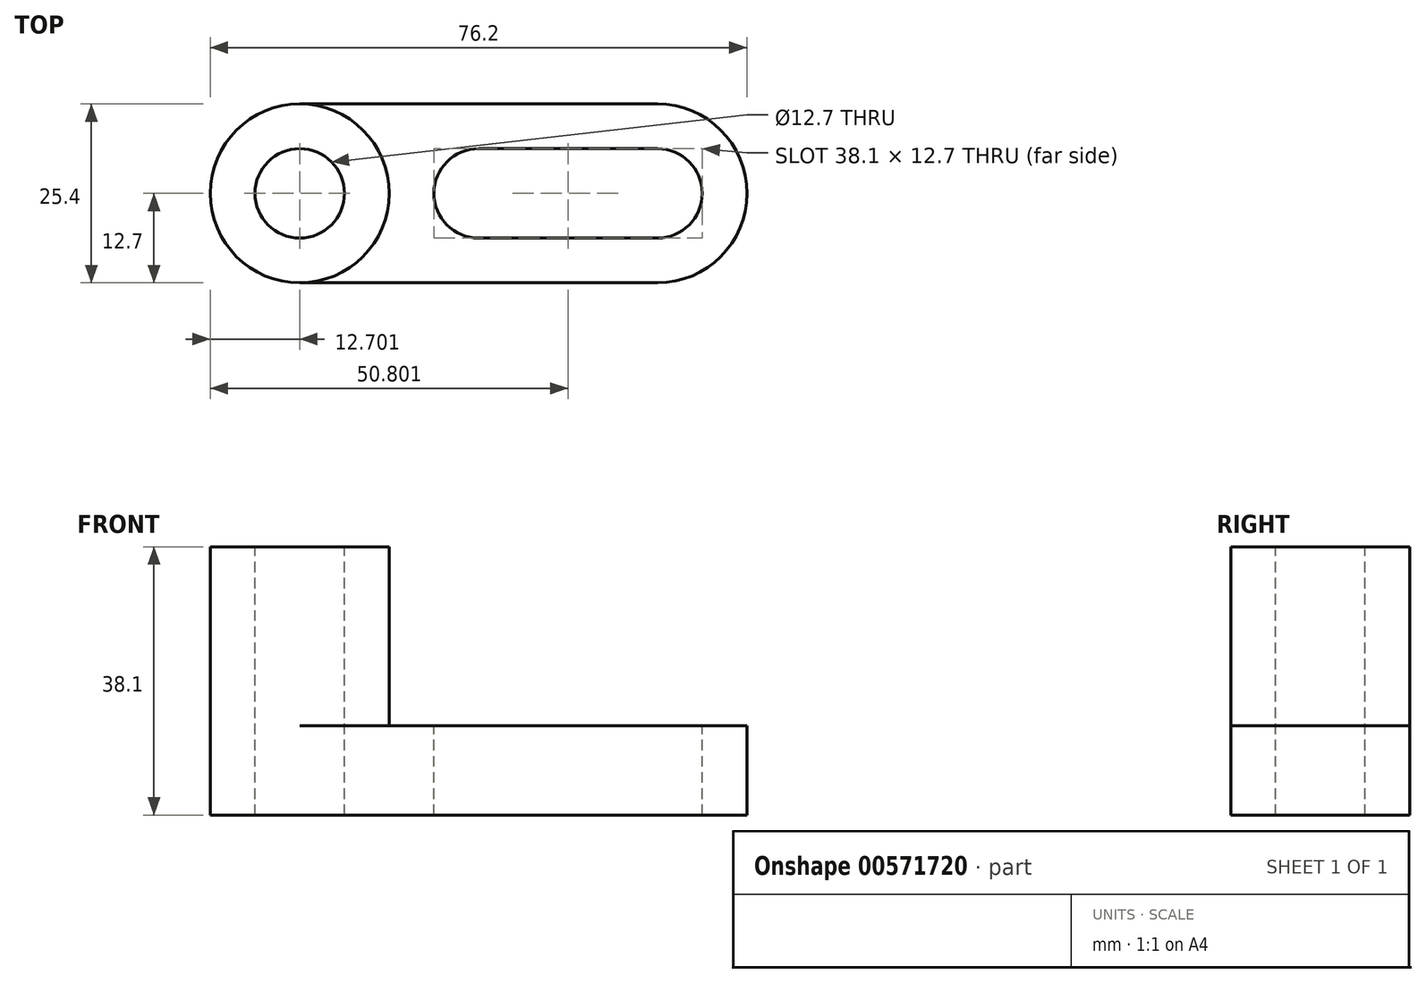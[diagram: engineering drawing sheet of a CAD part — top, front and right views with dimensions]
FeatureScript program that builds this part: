
annotation { "Feature Type Name" : "Feature", "Feature Type Description" : "" }
export const myFeature = defineFeature(function(context is Context, id is Id, definition is map)
    precondition{}
    {
        {
            var Q0;
            Q0=qCreatedBy(makeId("Front.planeOp"),FACE);
            var sketch = newSketch(context, id + "F0", { "sketchPlane" : qUnion([Q0])});
            skLineSegment(sketch, "E0", {"start": v(-41.4, 37.42) * mm, "end": v(9.4, 37.42) * mm});
            skLineSegment(sketch, "E1", {"start": v(9.4, 37.42) * mm, "end": v(9.4, 24.72) * mm});
            skLineSegment(sketch, "E2", {"start": v(9.4, 24.72) * mm, "end": v(-41.4, 24.72) * mm});
            skLineSegment(sketch, "E3", {"start": v(-41.4, 24.72) * mm, "end": v(-41.4, 37.42) * mm});
            skSolve(sketch);
        }
        {
            var Q0;
            Q0=makeQuery(id+"F0.imprint","IMPRINT",FACE,{"disambiguationData":[TD([[makeQuery(id+"F0.imprint","IMPRINT",EDGE,{"derivedFrom":sQuery(id+"F0.wireOp",EDGE,"E0")}),-1.0]])]});
            extrude(context, id + "F1", {"entities" : qUnion([Q0]), "depth" : 25.4 * mm, "offsetDistance" : 25.4 * mm});
        }
        {
            var Q0;
            Q0=makeQuery(id+"F1.opExtrude","SWEPT_FACE",FACE,{"disambiguationData":[OSD([sQuery(id+"F0.wireOp",EDGE,"E0")])]});
            var sketch = newSketch(context, id + "F2", { "sketchPlane" : qUnion([Q0])});
            skArc(sketch, "E4", {"start": v(9.4, -25.4) * mm, "mid": v(22.1, -12.7) * mm, "end": v(9.4, 0) * mm});
            skArc(sketch, "E5", {"start": v(-41.4, 0) * mm, "mid": v(-54.1, -12.7) * mm, "end": v(-41.4, -25.4) * mm});
            skCircle(sketch, "E6", {"center": v(-41.4, -12.7) * mm, "radius": 12.7 * mm});
            skSolve(sketch);
        }
        {
            var Q0;
            Q0=makeQuery(id+"F2.imprint","IMPRINT",FACE,{"disambiguationData":[TD([[makeQuery(id+"F2.imprint","IMPRINT",EDGE,{"derivedFrom":sQuery(id+"F2.wireOp",EDGE,"E4")}),1.0]])]});
            var Q1;
            {var subQ1=sQuery(id+"F0.wireOp",EDGE,"E0");var subQ2=makeQuery(id+"F1.opExtrude","SWEPT_EDGE",EDGE,{"disambiguationData":[OSD([subQ1,sQuery(id+"F0.wireOp",EDGE,"E3")])]});Q1=makeQuery(id+"F2.imprint","IMPRINT",FACE,{"disambiguationData":[TD([[makeQuery(id+"F2.imprint","IMPRINT",EDGE,{"derivedFrom":subQ2}),1.0]])]});}
            extrude(context, id + "F3", {"entities" : qUnion([Q0, Q1]), "operationType" : NewBodyOperationType.ADD, "oppositeDirection" : true, "depth" : 12.7 * mm, "offsetDistance" : 25.4 * mm});
        }
        {
            var Q0;
            Q0 = qSketchRegion(id + "F2", true);
            extrude(context, id + "F4", {"entities" : qUnion([Q0]), "operationType" : NewBodyOperationType.ADD, "depth" : 25.4 * mm, "offsetDistance" : 25.4 * mm});
        }
        {
            var Q0;
            Q0=makeQuery(id+"F4.opExtrude","CAP_FACE",FACE,{"disambiguationData":[OSD([sQuery(id+"F2.wireOp",EDGE,"E6")])],"isStart":false});
            var sketch = newSketch(context, id + "F5", { "sketchPlane" : qUnion([Q0])});
            skCircle(sketch, "E7", {"center": v(-41.4, -12.7) * mm, "radius": 6.35 * mm});
            skSolve(sketch);
        }
        {
            var Q0;
            Q0 = qSketchRegion(id + "F5", true);
            extrude(context, id + "F6", {"entities" : qUnion([Q0]), "operationType" : NewBodyOperationType.REMOVE, "oppositeDirection" : true, "depth" : 2514.6 * mm, "offsetDistance" : 25.4 * mm});
        }
        {
            var Q0;
            {var subQ0=sQuery(id+"F0.wireOp",EDGE,"E0");Q0=makeQuery(id+"F3.boolean.opBoolean","MERGE",FACE,{"derivedFrom":[makeQuery(id+"F1.opExtrude","SWEPT_FACE",FACE,{"disambiguationData":[OSD([subQ0])]}),makeQuery(id+"F3.opExtrude","CAP_FACE",FACE,{"disambiguationData":[OSD([subQ0,sQuery(id+"F0.wireOp",EDGE,"E1"),sQuery(id+"F2.wireOp",EDGE,"E4")])],"isStart":true}),makeQuery(id+"F3.opExtrude","CAP_FACE",FACE,{"disambiguationData":[OSD([subQ0,sQuery(id+"F0.wireOp",EDGE,"E3"),sQuery(id+"F2.wireOp",EDGE,"E6")])],"isStart":true})]});}
            var sketch = newSketch(context, id + "F7", { "sketchPlane" : qUnion([Q0])});
            skLineSegment(sketch, "E8", {"start": v(-16, -19.05) * mm, "end": v(9.4, -19.05) * mm});
            skLineSegment(sketch, "E9", {"start": v(-16, -19.05) * mm, "end": v(-16, -6.35) * mm});
            skLineSegment(sketch, "E10", {"start": v(-16, -6.35) * mm, "end": v(9.4, -6.35) * mm});
            skLineSegment(sketch, "E11", {"start": v(9.4, -6.35) * mm, "end": v(9.4, -19.05) * mm});
            skArc(sketch, "E12", {"start": v(-16, -6.35) * mm, "mid": v(-22.35, -12.7) * mm, "end": v(-16, -19.05) * mm});
            skArc(sketch, "E13", {"start": v(9.4, -19.05) * mm, "mid": v(15.75, -12.7) * mm, "end": v(9.4, -6.35) * mm});
            skSolve(sketch);
        }
        {
            var Q0;
            Q0=makeQuery(id+"F7.imprint","IMPRINT",FACE,{"disambiguationData":[TD([[makeQuery(id+"F7.imprint","IMPRINT",EDGE,{"derivedFrom":sQuery(id+"F7.wireOp",EDGE,"E8")}),1.0]])]});
            var Q1;
            Q1=makeQuery(id+"F7.imprint","IMPRINT",FACE,{"disambiguationData":[TD([[makeQuery(id+"F7.imprint","IMPRINT",EDGE,{"derivedFrom":sQuery(id+"F7.wireOp",EDGE,"E9")}),1.0]])]});
            var Q2;
            Q2=makeQuery(id+"F7.imprint","IMPRINT",FACE,{"disambiguationData":[TD([[makeQuery(id+"F7.imprint","IMPRINT",EDGE,{"derivedFrom":sQuery(id+"F7.wireOp",EDGE,"E11")}),1.0]])]});
            extrude(context, id + "F8", {"entities" : qUnion([Q0, Q1, Q2]), "operationType" : NewBodyOperationType.REMOVE, "oppositeDirection" : true, "depth" : 25.4 * mm, "offsetDistance" : 25.4 * mm});
        }
    });
